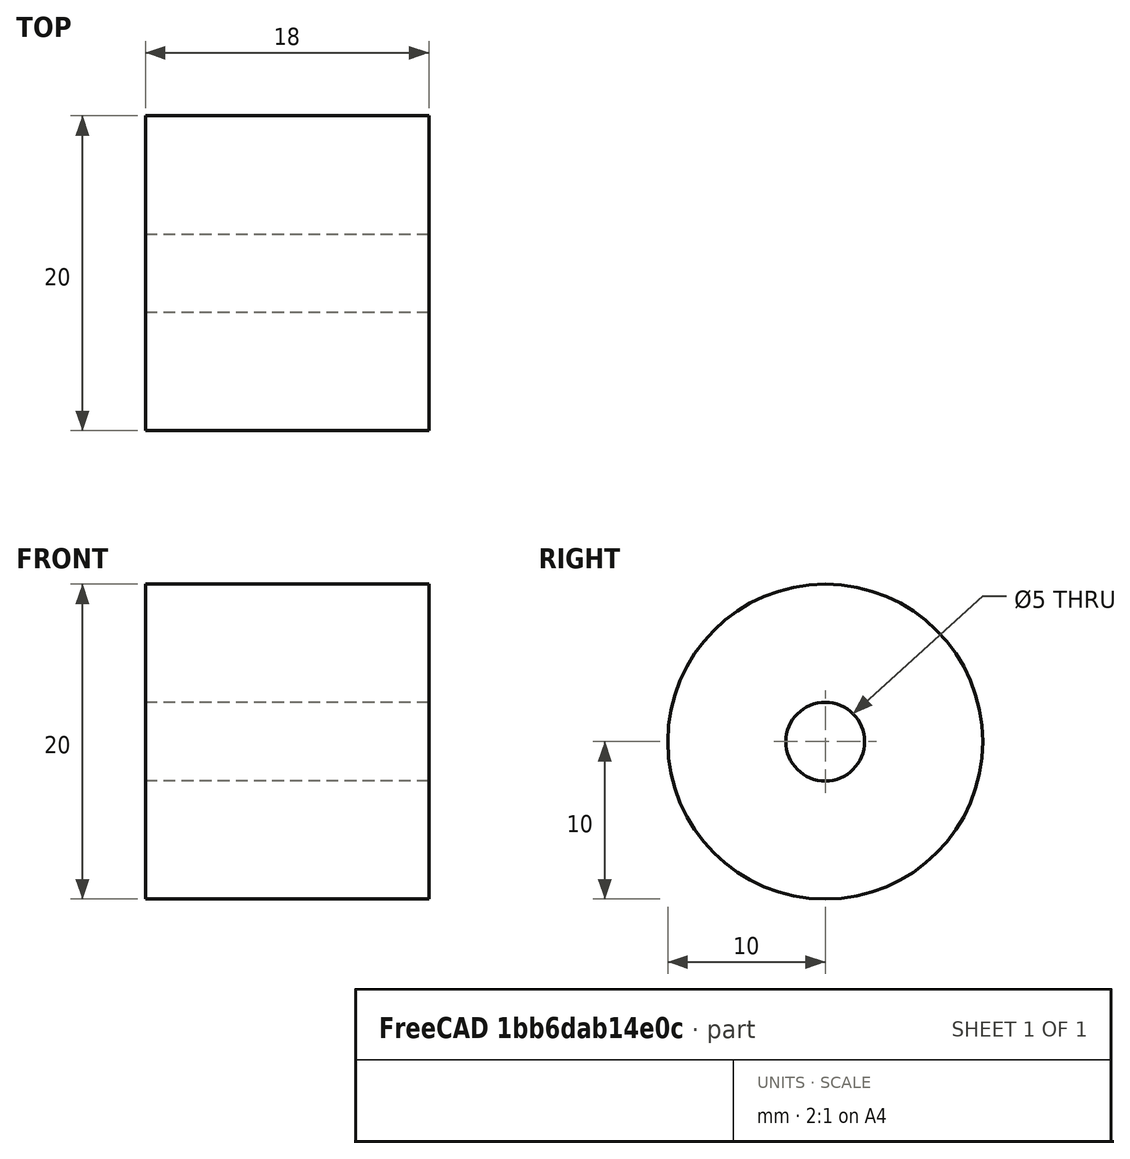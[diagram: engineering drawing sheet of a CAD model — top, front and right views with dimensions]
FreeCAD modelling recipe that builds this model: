
FCSTD DOCUMENT  (FreeCAD 0.19R21911 +2545 (Git))
Label: slizgacz
License: All rights reserved
LicenseURL: http://en.wikipedia.org/wiki/All_rights_reserved
objects: Sketcher::SketchObject×1, PartDesign::Pad×1, PartDesign::Line×1, PartDesign::Body×1
note: 6 computed .brp shape members not serialized (recipe doc carries the construction recipe); baked Part::Feature solids carry a one-line shape summary decoded from their .brp

FEATURE [Sketcher::SketchObject] Sketch
  MapMode = 5
  Placement = pos=(0,0,0) rot=(0.57735,0.57735,0.57735;2.0944rad)
  Support = -> [YZ_Plane]
  sketch-geometry (2):
    g0: Circle CenterX=0 CenterY=0 CenterZ=0 NormalX=0 NormalY=0 NormalZ=1 AngleXU=0 Radius=10
    g1: Circle CenterX=0 CenterY=0 CenterZ=0 NormalX=0 NormalY=0 NormalZ=1 AngleXU=0 Radius=2.5
  constraints (4):
    c: Coincident(g0,g-1)
    c: Coincident(g1,g0)
    c: Radius(g1) = 2.5
    c: Radius(g0) = 10
FEATURE [PartDesign::Pad] Pad
  AllowMultiFace = false
  ClaimChildren = false
  Length = 18
  Length2 = 100
  Placement = pos=(0,0,0) rot=(0.57735,0.57735,0.57735;2.0944rad)
  Profile = -> Sketch
  Suppress = false
  Type = 0
FEATURE [PartDesign::Line] DatumLine
  AttacherType = Attacher::AttachEngineLine
  Length = 18
  MapMode = 42
  Placement = pos=(0,9e-16,5e-16) rot=(0.57735,0.57735,0.57735;2.0944rad)
  ResizeMode = 0
  Support = -> [Pad]
FEATURE [PartDesign::Body] Body  label="slizgacz"
  ExportMode = 0
  Group = -> [Sketch,Pad,DatumLine]
  Origin = -> Origin
  SingleSolid = true
  Tip = -> Pad
  _ExportChildren = -> [Pad,DatumLine]
  _GroupVersion = 1
